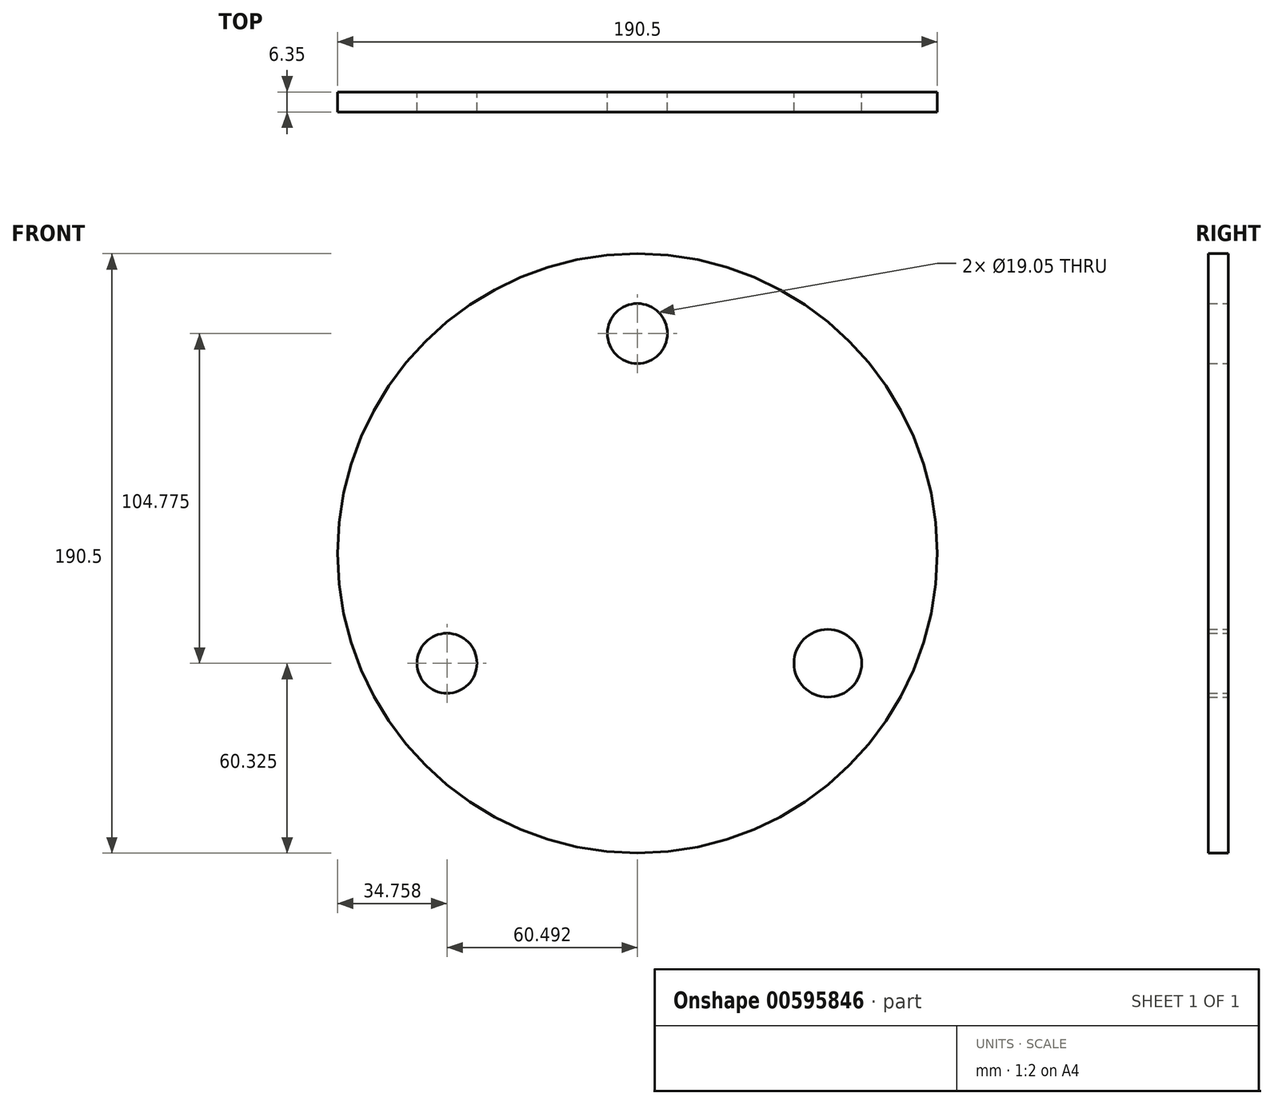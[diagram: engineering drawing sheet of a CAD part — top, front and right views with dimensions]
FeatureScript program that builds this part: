
annotation { "Feature Type Name" : "Feature", "Feature Type Description" : "" }
export const myFeature = defineFeature(function(context is Context, id is Id, definition is map)
    precondition{}
    {
        {
            var Q0;
            Q0=qCreatedBy(makeId("Front.planeOp"),FACE);
            var sketch = newSketch(context, id + "F0", { "sketchPlane" : qUnion([Q0])});
            skCircle(sketch, "E0", {"center": v(0, 0) * mm, "radius": 95.25 * mm});
            skSolve(sketch);
        }
        {
            var Q0;
            Q0 = qSketchRegion(id + "F0", true);
            extrude(context, id + "F1", {"entities" : qUnion([Q0]), "depth" : 6.35 * mm, "offsetDistance" : 25.4 * mm});
        }
        {
            var Q0;
            Q0=qCreatedBy(makeId("Front.planeOp"),FACE);
            var sketch = newSketch(context, id + "F2", { "sketchPlane" : qUnion([Q0])});
            skCircle(sketch, "E1", {"center": v(0, 0) * mm, "radius": 69.85 * mm, "construction": true});
            skCircle(sketch, "E2", {"center": v(0, 69.85) * mm, "radius": 9.53 * mm});
            skCircle(sketch, "E3", {"center": v(-60.5, -34.92) * mm, "radius": 9.53 * mm});
            skLineSegment(sketch, "E4", {"start": v(-60.5, -34.92) * mm, "end": v(60.5, -34.92) * mm, "construction": true});
            skCircle(sketch, "E5", {"center": v(60.5, -34.92) * mm, "radius": 10.75 * mm});
            skLineSegment(sketch, "E6", {"start": v(-60.5, -34.93) * mm, "end": v(0, 69.85) * mm, "construction": true});
            skLineSegment(sketch, "E7", {"start": v(0, 69.85) * mm, "end": v(60.5, -34.93) * mm, "construction": true});
            skSolve(sketch);
        }
        {
            var Q0;
            Q0 = qSketchRegion(id + "F2", true);
            extrude(context, id + "F3", {"entities" : qUnion([Q0]), "operationType" : NewBodyOperationType.REMOVE, "endBound" : BoundingType.UP_TO_NEXT, "depth" : 25.4 * mm, "offsetDistance" : 25.4 * mm});
        }
    });
